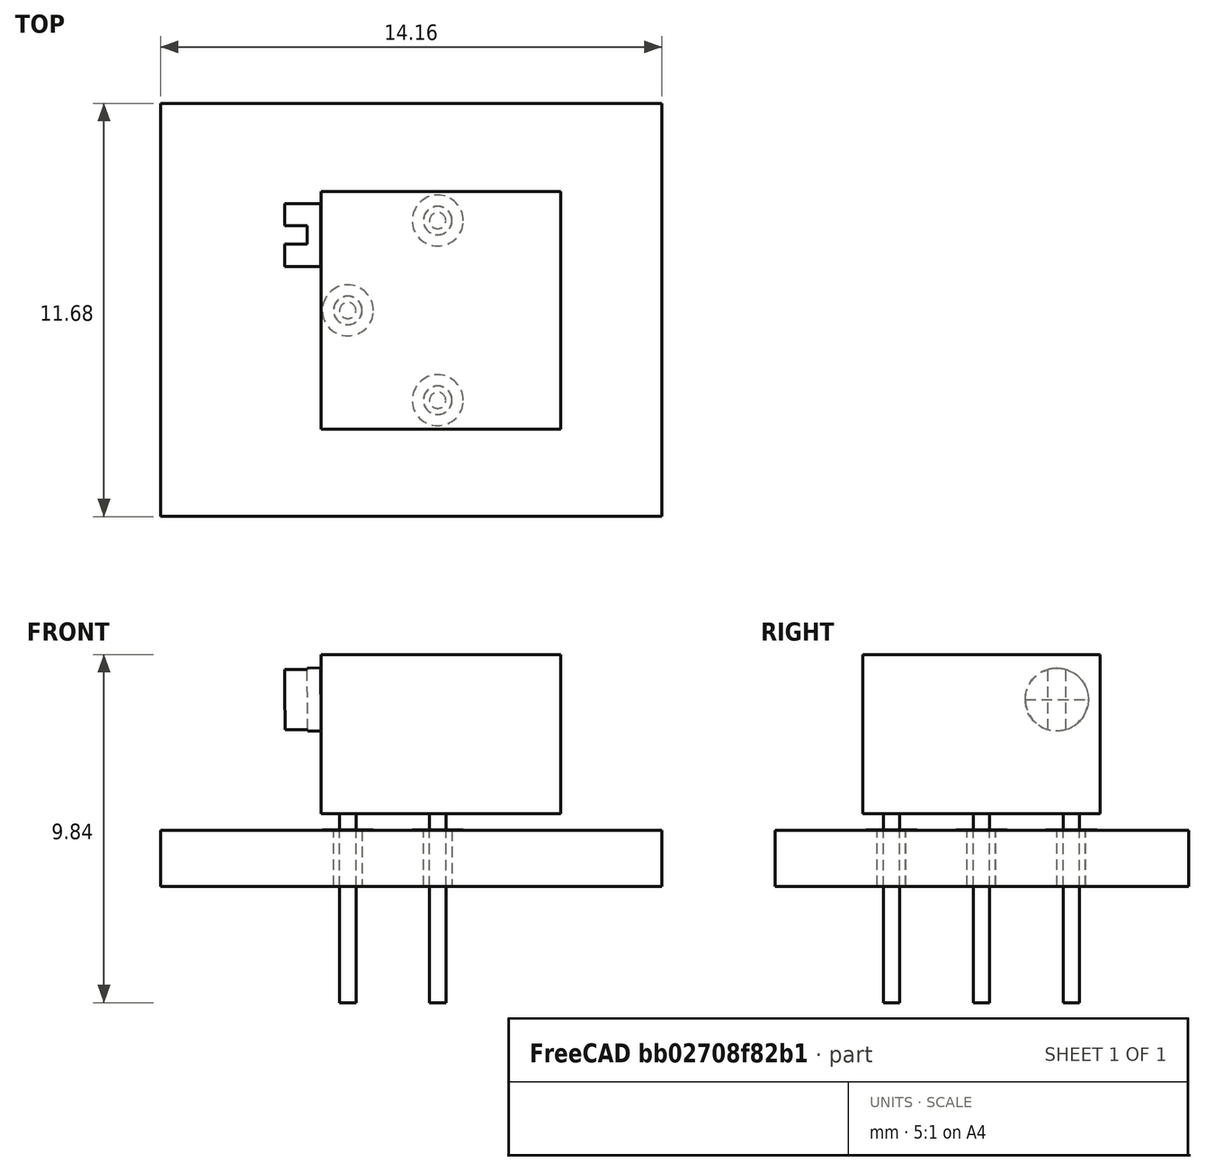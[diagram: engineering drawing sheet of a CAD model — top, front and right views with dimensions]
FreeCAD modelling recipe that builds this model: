
FCSTD DOCUMENT  (FreeCAD 0.18R15611 (Git))
Label: Potentiometer_Bourns_3266P_Horizontal
License: All rights reserved
LicenseURL: http://en.wikipedia.org/wiki/All_rights_reserved
objects: Part::FeaturePython×7, Part::Cylinder×4, Part::Box×2, App::DocumentObjectGroup×1, Part::Cut×1, Part::MultiFuse×1, Part::Feature×1
note: 16 computed .brp shape members not serialized (recipe doc carries the construction recipe); baked Part::Feature solids carry a one-line shape summary decoded from their .brp

FEATURE [Part::FeaturePython] FCrtYd_lines  label="FCrtYd"  # a2plus imported part (geometry in sourceFile) (typed FeaturePython)
  fixedPosition = true
FEATURE [Part::FeaturePython] FFab_lines  label="FFab"  # a2plus imported part (geometry in sourceFile) (typed FeaturePython)
  fixedPosition = true
FEATURE [Part::FeaturePython] Filk_lines  label="FrontSilk"  # a2plus imported part (geometry in sourceFile) (typed FeaturePython)
  fixedPosition = true
FEATURE [Part::FeaturePython] TopPads  # a2plus imported part (geometry in sourceFile) (typed FeaturePython)
  fixedPosition = true
FEATURE [Part::FeaturePython] BotPads  # a2plus imported part (geometry in sourceFile) (typed FeaturePython)
  fixedPosition = true
FEATURE [Part::FeaturePython] THPs  label="PTHs"  # a2plus imported part (geometry in sourceFile) (typed FeaturePython)
  fixedPosition = true
FEATURE [Part::FeaturePython] newPCB  label="Pcb"  # a2plus imported part (geometry in sourceFile) (typed FeaturePython)
  fixedPosition = true
FEATURE [App::DocumentObjectGroup] Potentiometer_Bourns_3266P_Horizontal_fp
  Group = -> [FCrtYd_lines,FFab_lines,Filk_lines,TopPads,BotPads,THPs,newPCB]
FEATURE [Part::Cylinder] Cylinder001  label="Pin3"
  Angle = 360
  AttacherType = Attacher::AttachEngine3D
  Height = 5.34
  Placement = pos=(0,-5.08,-4.88) rot=(0,0,1;0rad)
  Radius = 0.23
FEATURE [Part::Cylinder] Cylinder002  label="Pin2"
  Angle = 360
  AttacherType = Attacher::AttachEngine3D
  Height = 5.34
  Placement = pos=(-2.54,-2.54,-4.88) rot=(0,0,1;0rad)
  Radius = 0.23
FEATURE [Part::Cylinder] Cylinder  label="Pin1"
  Angle = 360
  AttacherType = Attacher::AttachEngine3D
  Height = 5.34
  Placement = pos=(0,0,-4.88) rot=(0,0,1;0rad)
  Radius = 0.23
FEATURE [Part::Box] Box  label="Body"
  AttacherType = Attacher::AttachEngine3D
  Height = 4.5
  Length = 6.78
  Placement = pos=(-3.3,-5.895,0.46) rot=(0,0,1;0rad)
  Width = 6.71
FEATURE [Part::Cylinder] Cylinder003  label="Knob"
  Angle = 360
  AttacherType = Attacher::AttachEngine3D
  Height = 1.02
  Placement = pos=(-0.405,-2.25,7.24) rot=(0,0,1;0rad)
  Radius = 0.89
FEATURE [Part::Box] Box003  label="Cube001"
  AttacherType = Attacher::AttachEngine3D
  Height = 0.64
  Length = 10
  Placement = pos=(-5,-2.5,7.62) rot=(0,0,1;0rad)
  Width = 0.51
FEATURE [Part::Cut] Cut  label="CutKnob"
  Base = -> Cylinder003
  Placement = pos=(3.93629,1.84,4.16) rot=(0,-1,0;1.57931rad)
  Refine = true
  Tool = -> Box003
FEATURE [Part::MultiFuse] Pin1_mp_cp  label="Pin1_fd"
  Refine = true
  Shapes = -> [Cylinder,Box,Cut,Cylinder002,Cylinder001]
FEATURE [Part::Feature] Shape001  label="Potentiometer_Bourns_3266P_Horizontal"
  shape: bbox 7.808 x 6.71 x 9.84 mm, 19 faces (baked)
